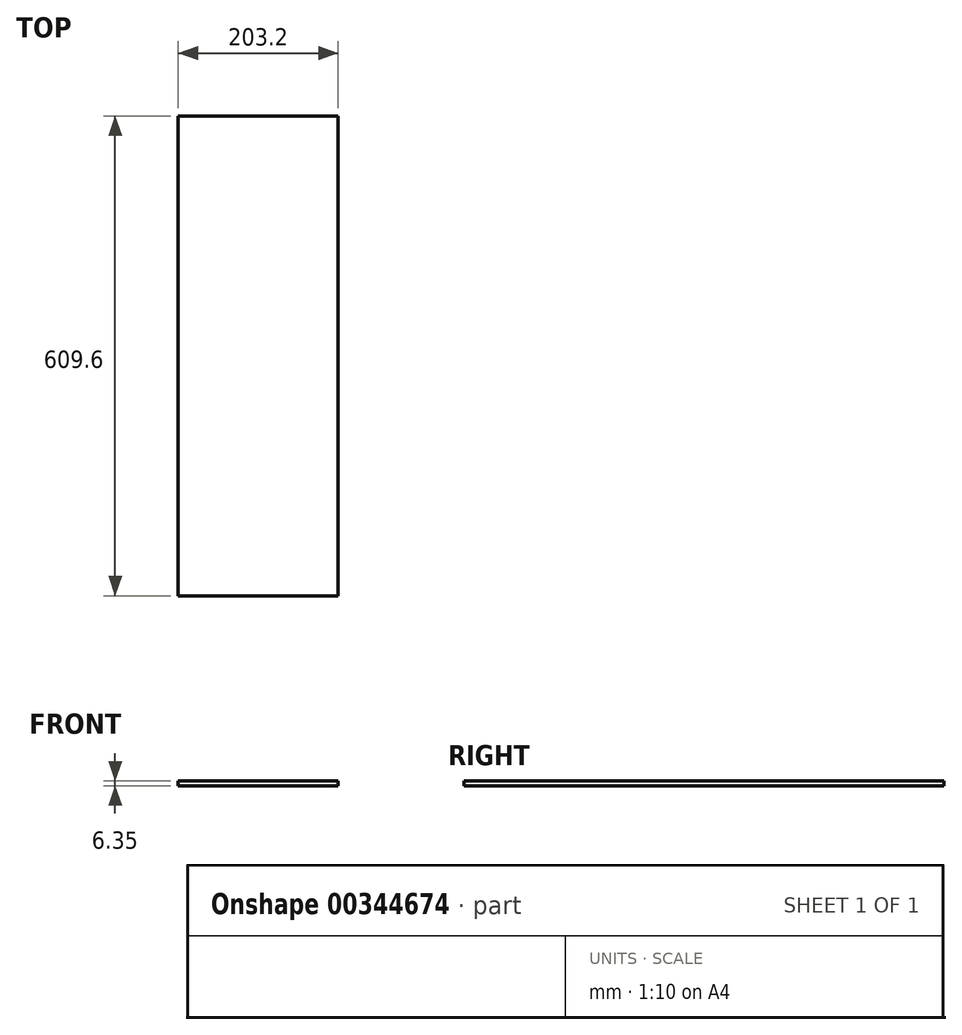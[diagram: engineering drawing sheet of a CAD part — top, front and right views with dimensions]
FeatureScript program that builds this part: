
annotation { "Feature Type Name" : "Feature", "Feature Type Description" : "" }
export const myFeature = defineFeature(function(context is Context, id is Id, definition is map)
    precondition{}
    {
        {
            var Q0;
            Q0=qCreatedBy(makeId("Top.planeOp"),FACE);
            var sketch = newSketch(context, id + "F0", { "sketchPlane" : qUnion([Q0])});
            skLineSegment(sketch, "E0.bottom", {"start": v(0, 0) * mm, "end": v(203.2, 0) * mm});
            skLineSegment(sketch, "E0.top", {"start": v(0, 609.6) * mm, "end": v(203.2, 609.6) * mm});
            skLineSegment(sketch, "E0.left", {"start": v(0, 0) * mm, "end": v(0, 609.6) * mm});
            skLineSegment(sketch, "E0.right", {"start": v(203.2, 0) * mm, "end": v(203.2, 609.6) * mm});
            skSolve(sketch);
        }
        {
            var Q0;
            Q0=makeQuery(id+"F0.imprint","IMPRINT",FACE,{"disambiguationData":[TD([[makeQuery(id+"F0.imprint","IMPRINT",EDGE,{"derivedFrom":sQuery(id+"F0.wireOp",EDGE,"E0.bottom")}),1.0]])]});
            extrude(context, id + "F1", {"entities" : qUnion([Q0]), "depth" : 6.35 * mm});
        }
    });
